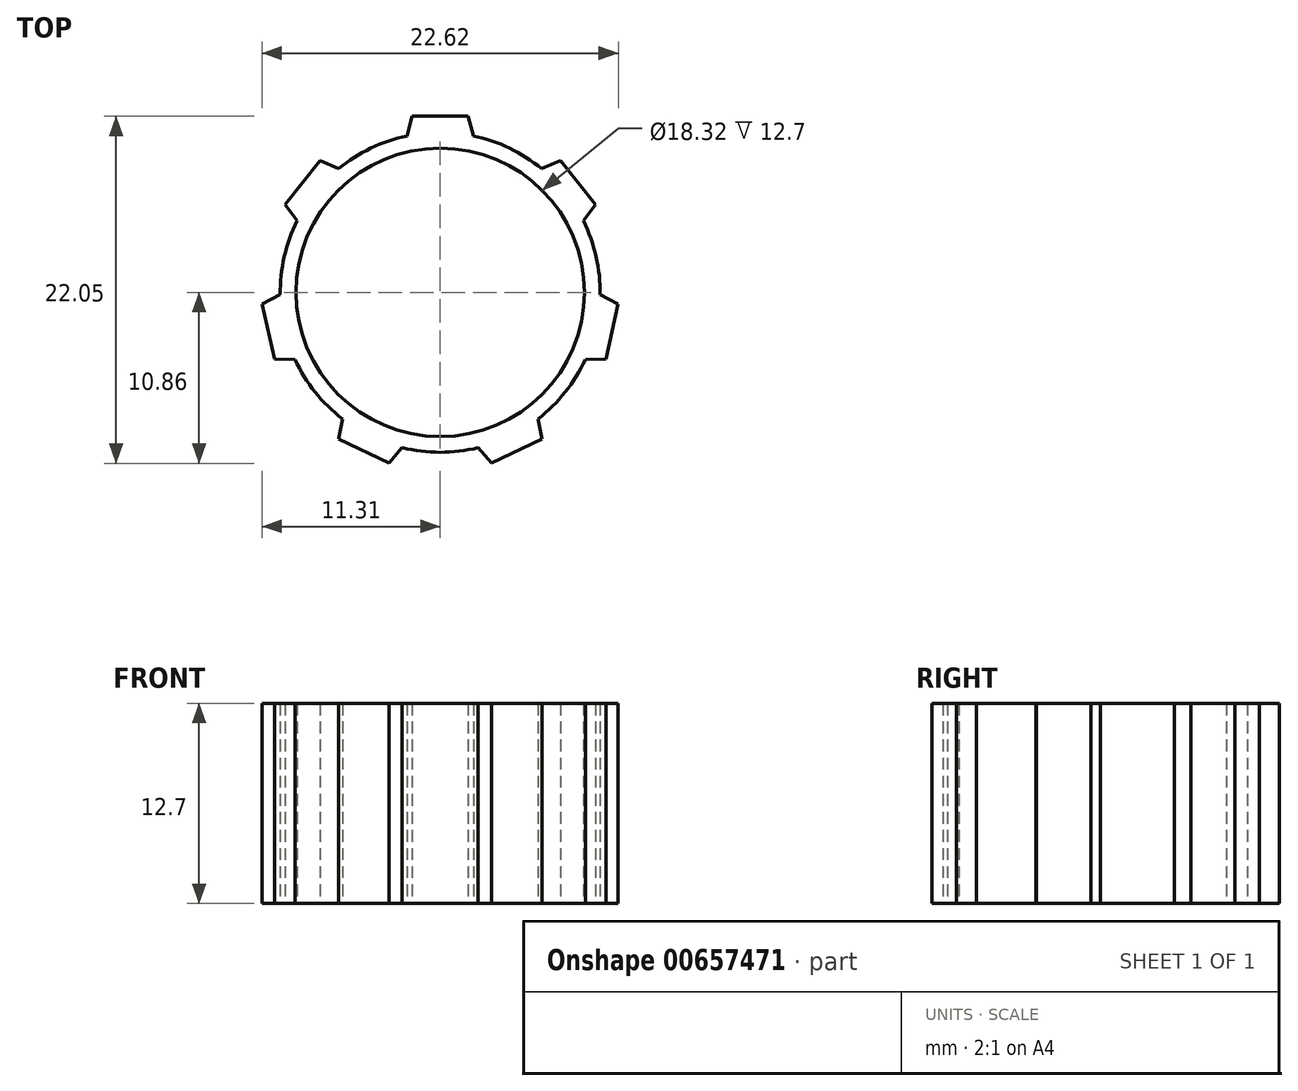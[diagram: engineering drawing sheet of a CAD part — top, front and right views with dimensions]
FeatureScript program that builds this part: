
annotation { "Feature Type Name" : "Feature", "Feature Type Description" : "" }
export const myFeature = defineFeature(function(context is Context, id is Id, definition is map)
    precondition{}
    {
        {
            var Q0;
            Q0=qCreatedBy(makeId("Top.planeOp"),FACE);
            var sketch = newSketch(context, id + "F0", { "sketchPlane" : qUnion([Q0])});
            skCircle(sketch, "E0", {"center": v(0, 0) * mm, "radius": 9.16 * mm});
            skLineSegment(sketch, "E1", {"start": v(2.11, 9.94) * mm, "end": v(1.78, 11.2) * mm});
            skLineSegment(sketch, "E2", {"start": v(1.78, 11.2) * mm, "end": v(0, 11.2) * mm});
            skLineSegment(sketch, "E3", {"start": v(0, 11.2) * mm, "end": v(0, 10.16) * mm, "construction": true});
            skLineSegment(sketch, "E4.MirrorCS", {"start": v(-1.78, 11.2) * mm, "end": v(0, 11.2) * mm});
            skLineSegment(sketch, "E5.MirrorCS", {"start": v(-2.11, 9.94) * mm, "end": v(-1.78, 11.2) * mm});
            skLineSegment(sketch, "E6.1.0", {"start": v(-6.45, 7.85) * mm, "end": v(-7.64, 8.37) * mm});
            skLineSegment(sketch, "E6.1.1", {"start": v(-7.64, 8.37) * mm, "end": v(-8.75, 6.98) * mm});
            skLineSegment(sketch, "E6.1.2", {"start": v(-9.86, 5.59) * mm, "end": v(-8.75, 6.98) * mm});
            skLineSegment(sketch, "E6.1.3", {"start": v(-9.09, 4.54) * mm, "end": v(-9.09, 4.54) * mm});
            skLineSegment(sketch, "E6.2.0", {"start": v(-10.16, -0.15) * mm, "end": v(-11.3, -0.76) * mm});
            skLineSegment(sketch, "E6.2.1", {"start": v(-11.3, -0.76) * mm, "end": v(-10.91, -2.5) * mm});
            skLineSegment(sketch, "E6.2.2", {"start": v(-10.52, -4.22) * mm, "end": v(-10.91, -2.5) * mm});
            skLineSegment(sketch, "E6.2.3", {"start": v(-9.22, -4.27) * mm, "end": v(-9.22, -4.27) * mm});
            skLineSegment(sketch, "E6.3.0", {"start": v(-6.22, -8.04) * mm, "end": v(-6.46, -9.31) * mm});
            skLineSegment(sketch, "E6.3.1", {"start": v(-6.46, -9.31) * mm, "end": v(-4.86, -10.08) * mm});
            skLineSegment(sketch, "E6.3.2", {"start": v(-3.25, -10.86) * mm, "end": v(-4.86, -10.08) * mm});
            skLineSegment(sketch, "E6.3.3", {"start": v(-2.4, -9.87) * mm, "end": v(-3.25, -10.86) * mm});
            skLineSegment(sketch, "E6.4.0", {"start": v(2.4, -9.87) * mm, "end": v(3.25, -10.86) * mm});
            skLineSegment(sketch, "E6.4.1", {"start": v(3.25, -10.86) * mm, "end": v(4.86, -10.08) * mm});
            skLineSegment(sketch, "E6.4.2", {"start": v(6.46, -9.31) * mm, "end": v(4.86, -10.08) * mm});
            skLineSegment(sketch, "E6.4.3", {"start": v(6.22, -8.04) * mm, "end": v(6.22, -8.04) * mm});
            skLineSegment(sketch, "E6.5.0", {"start": v(9.22, -4.27) * mm, "end": v(10.52, -4.22) * mm});
            skLineSegment(sketch, "E6.5.1", {"start": v(10.52, -4.22) * mm, "end": v(10.91, -2.5) * mm});
            skLineSegment(sketch, "E6.5.2", {"start": v(11.3, -0.76) * mm, "end": v(10.91, -2.5) * mm});
            skLineSegment(sketch, "E6.5.3", {"start": v(10.16, -0.15) * mm, "end": v(11.3, -0.76) * mm});
            skLineSegment(sketch, "E6.6.0", {"start": v(9.09, 4.54) * mm, "end": v(9.86, 5.59) * mm});
            skLineSegment(sketch, "E6.6.1", {"start": v(9.86, 5.59) * mm, "end": v(8.75, 6.98) * mm});
            skLineSegment(sketch, "E6.6.2", {"start": v(7.64, 8.37) * mm, "end": v(8.75, 6.98) * mm});
            skLineSegment(sketch, "E6.6.3", {"start": v(6.45, 7.85) * mm, "end": v(7.64, 8.37) * mm});
            skArc(sketch, "E7", {"start": v(2.11, 9.94) * mm, "mid": v(0, 10.16) * mm, "end": v(-2.11, 9.94) * mm, "construction": true});
            skArc(sketch, "E8", {"start": v(-2.11, 9.94) * mm, "mid": v(-4.4, 9.15) * mm, "end": v(-6.45, 7.85) * mm});
            skArc(sketch, "E9", {"start": v(-6.45, 7.85) * mm, "mid": v(-7.94, 6.33) * mm, "end": v(-9.09, 4.54) * mm, "construction": true});
            skLineSegment(sketch, "E10", {"start": v(-9.09, 4.54) * mm, "end": v(-9.86, 5.59) * mm});
            skArc(sketch, "E11", {"start": v(-10.16, -0.15) * mm, "mid": v(-9.9, -2.26) * mm, "end": v(-9.22, -4.27) * mm, "construction": true});
            skLineSegment(sketch, "E12", {"start": v(-9.22, -4.27) * mm, "end": v(-10.52, -4.22) * mm});
            skArc(sketch, "E13", {"start": v(-6.22, -8.04) * mm, "mid": v(-4.4, -9.15) * mm, "end": v(-2.4, -9.87) * mm, "construction": true});
            skArc(sketch, "E14", {"start": v(-2.4, -9.87) * mm, "mid": v(0, -10.16) * mm, "end": v(2.4, -9.87) * mm});
            skArc(sketch, "E15", {"start": v(2.4, -9.87) * mm, "mid": v(4.4, -9.15) * mm, "end": v(6.22, -8.04) * mm, "construction": true});
            skArc(sketch, "E16", {"start": v(9.22, -4.27) * mm, "mid": v(9.9, -2.26) * mm, "end": v(10.16, -0.15) * mm, "construction": true});
            skArc(sketch, "E17", {"start": v(10.16, -0.15) * mm, "mid": v(9.9, 2.26) * mm, "end": v(9.09, 4.54) * mm});
            skArc(sketch, "E18", {"start": v(9.09, 4.54) * mm, "mid": v(7.94, 6.33) * mm, "end": v(6.45, 7.85) * mm, "construction": true});
            skArc(sketch, "E19", {"start": v(6.45, 7.85) * mm, "mid": v(4.4, 9.15) * mm, "end": v(2.11, 9.94) * mm});
            skArc(sketch, "E20", {"start": v(-9.09, 4.54) * mm, "mid": v(-9.9, 2.26) * mm, "end": v(-10.16, -0.15) * mm});
            skArc(sketch, "E21", {"start": v(-9.22, -4.27) * mm, "mid": v(-7.94, -6.33) * mm, "end": v(-6.22, -8.04) * mm});
            skLineSegment(sketch, "E22", {"start": v(6.22, -8.04) * mm, "end": v(6.46, -9.31) * mm});
            skArc(sketch, "E23", {"start": v(6.22, -8.04) * mm, "mid": v(7.94, -6.33) * mm, "end": v(9.22, -4.27) * mm});
            skSolve(sketch);
        }
        {
            var Q0;
            Q0=makeQuery(id+"F0.imprint","IMPRINT",FACE,{"disambiguationData":[TD([[makeQuery(id+"F0.imprint","IMPRINT",EDGE,{"derivedFrom":sQuery(id+"F0.wireOp",EDGE,"E0")}),-1.0]])]});
            extrude(context, id + "F1", {"entities" : qUnion([Q0]), "depth" : 12.7 * mm, "offsetDistance" : 25.4 * mm});
        }
    });
